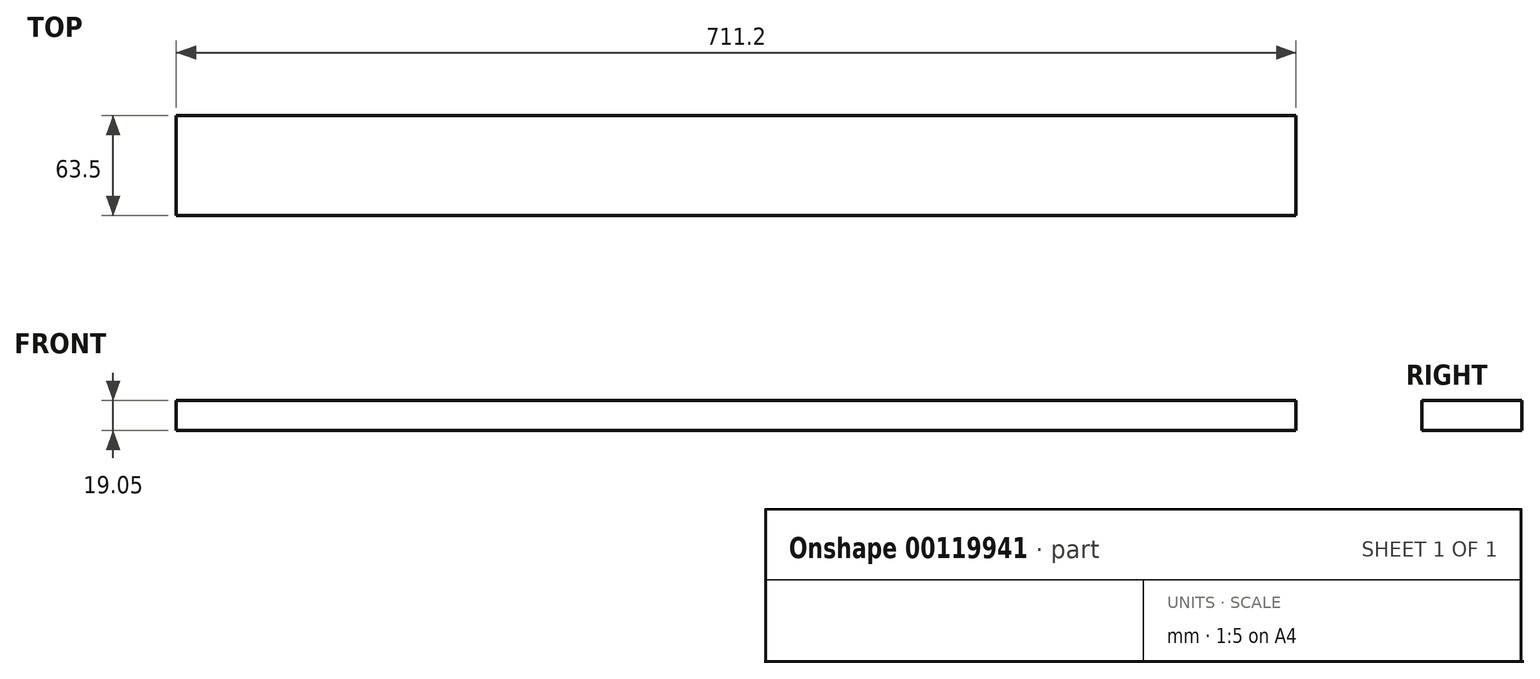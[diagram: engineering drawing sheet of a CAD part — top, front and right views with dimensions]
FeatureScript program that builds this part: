
annotation { "Feature Type Name" : "Feature", "Feature Type Description" : "" }
export const myFeature = defineFeature(function(context is Context, id is Id, definition is map)
    precondition{}
    {
        {
            var Q0;
            Q0=qCreatedBy(makeId("Top.planeOp"),FACE);
            var sketch = newSketch(context, id + "F0", { "sketchPlane" : qUnion([Q0])});
            skLineSegment(sketch, "E0.bottom", {"start": v(0, 0) * mm, "end": v(711.2, 0) * mm});
            skLineSegment(sketch, "E0.top", {"start": v(0, 63.5) * mm, "end": v(711.2, 63.5) * mm});
            skLineSegment(sketch, "E0.left", {"start": v(0, 0) * mm, "end": v(0, 63.5) * mm});
            skLineSegment(sketch, "E0.right", {"start": v(711.2, 0) * mm, "end": v(711.2, 63.5) * mm});
            skSolve(sketch);
        }
        {
            var Q0;
            Q0 = qSketchRegion(id + "F0", true);
            extrude(context, id + "F1", {"entities" : qUnion([Q0]), "depth" : 19.05 * mm});
        }
    });
